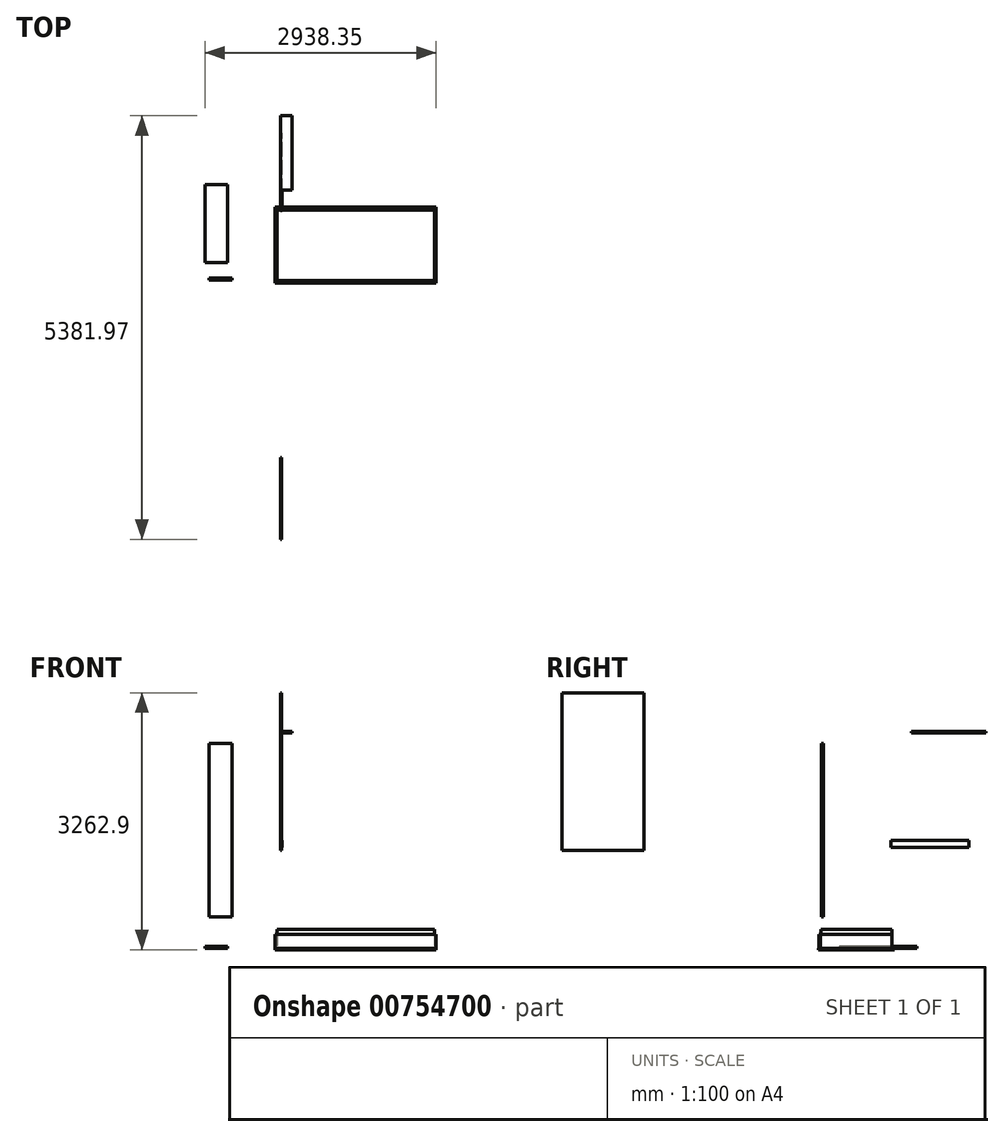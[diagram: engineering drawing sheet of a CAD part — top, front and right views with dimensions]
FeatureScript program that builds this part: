
annotation { "Feature Type Name" : "Feature", "Feature Type Description" : "" }
export const myFeature = defineFeature(function(context is Context, id is Id, definition is map)
    precondition{}
    {
        {
            assignVariable(context, id + "F0", {"name" : "MattD", "anyValue" : 240});
        }
        {
            assignVariable(context, id + "F1", {"name" : "BaseD", "anyValue" : 18});
        }
        {
            assignVariable(context, id + "F2", {"name" : "RailD", "anyValue" : 18});
        }
        {
            assignVariable(context, id + "F3", {"name" : "RailSOH", "anyValue" : 10});
        }
        {
            assignVariable(context, id + "F4", {"name" : "FrameD", "anyValue" : 24});
        }
        {
            var Q0;
            Q0=qCreatedBy(makeId("Top.planeOp"),FACE);
            var sketch = newSketch(context, id + "F5", { "sketchPlane" : qUnion([Q0])});
            skLineSegment(sketch, "E0.bottom", {"start": v(-44.22, 868.08) * mm, "end": v(1955.78, 868.08) * mm});
            skLineSegment(sketch, "E0.top", {"start": v(-44.22, -31.92) * mm, "end": v(1955.78, -31.92) * mm});
            skLineSegment(sketch, "E0.left", {"start": v(-44.22, 868.08) * mm, "end": v(-44.22, -31.92) * mm});
            skLineSegment(sketch, "E0.right", {"start": v(1955.78, 868.08) * mm, "end": v(1955.78, -31.92) * mm});
            skSolve(sketch);
        }
        {
            var Q0;
            Q0=makeQuery(id+"F5.imprint","IMPRINT",FACE,{"disambiguationData":[TD([[makeQuery(id+"F5.imprint","IMPRINT",EDGE,{"derivedFrom":sQuery(id+"F5.wireOp",EDGE,"E0.bottom")}),-1.0]])]});
            extrude(context, id + "F6", {"entities" : qUnion([Q0]), "depth" : (getVariable(context, 'MattD')) * mm, "offsetDistance" : 25 * mm});
        }
        {
            var Q0;
            Q0=qCreatedBy(makeId("Top.planeOp"),FACE);
            var sketch = newSketch(context, id + "F7", { "sketchPlane" : qUnion([Q0])});
            skLineSegment(sketch, "E1.bottom", {"start": v(-67.22, 901.08) * mm, "end": v(1978.78, 901.08) * mm});
            skLineSegment(sketch, "E1.top", {"start": v(-67.22, -64.92) * mm, "end": v(1978.78, -64.92) * mm});
            skLineSegment(sketch, "E1.left", {"start": v(-67.22, 901.08) * mm, "end": v(-67.22, -64.92) * mm});
            skLineSegment(sketch, "E1.right", {"start": v(1978.78, 901.08) * mm, "end": v(1978.78, -64.92) * mm});
            skSolve(sketch);
        }
        {
            var Q0;
            Q0=makeQuery(id+"F7.imprint","IMPRINT",FACE,{"disambiguationData":[TD([[makeQuery(id+"F7.imprint","IMPRINT",EDGE,{"derivedFrom":sQuery(id+"F7.wireOp",EDGE,"E1.bottom")}),-1.0]])]});
            extrude(context, id + "F8", {"entities" : qUnion([Q0]), "oppositeDirection" : true, "depth" : (getVariable(context, 'BaseD')) * mm, "offsetDistance" : 25 * mm});
        }
        {
            var Q0;
            Q0=makeQuery(id+"F8.opExtrude","SWEPT_FACE",FACE,{"disambiguationData":[OSD([sQuery(id+"F7.wireOp",EDGE,"E1.top")])]});
            cPlane(context, id + "F9", {"entities" : qUnion([Q0]), "cplaneType" : CPlaneType.OFFSET, "offset" : (getVariable(context, 'RailSOH')) * mm, "oppositeDirection" : true, "width" : 150 * mm, "height" : 150 * mm});
        }
        {
            var Q0;
            Q0=qCreatedBy(id+"F9.planeOp",FACE);
            var sketch = newSketch(context, id + "F10", { "sketchPlane" : qUnion([Q0])});
            skLineSegment(sketch, "E2.bottom", {"start": v(-67.22, 180) * mm, "end": v(1978.78, 180) * mm});
            skLineSegment(sketch, "E2.top", {"start": v(-67.22, 0) * mm, "end": v(1978.78, 0) * mm});
            skLineSegment(sketch, "E2.left", {"start": v(-67.22, 180) * mm, "end": v(-67.22, 0) * mm});
            skLineSegment(sketch, "E2.right", {"start": v(1978.78, 180) * mm, "end": v(1978.78, 0) * mm});
            skSolve(sketch);
        }
        {
            var Q0;
            Q0=makeQuery(id+"F10.imprint","IMPRINT",FACE,{"disambiguationData":[TD([[makeQuery(id+"F10.imprint","IMPRINT",EDGE,{"derivedFrom":sQuery(id+"F10.wireOp",EDGE,"E2.bottom")}),-1.0]])]});
            extrude(context, id + "F11", {"entities" : qUnion([Q0]), "oppositeDirection" : true, "depth" : (getVariable(context, 'RailD')) * mm, "offsetDistance" : 25 * mm});
        }
        {
            var Q0;
            Q0=makeQuery(id+"F11.opExtrude","SWEPT_FACE",FACE,{"disambiguationData":[OSD([sQuery(id+"F10.wireOp",EDGE,"E2.right")])]});
            var sketch = newSketch(context, id + "F12", { "sketchPlane" : qUnion([Q0])});
            skLineSegment(sketch, "E3.bottom", {"start": v(-36.92, 180) * mm, "end": v(873.08, 180) * mm});
            skLineSegment(sketch, "E3.top", {"start": v(-36.92, 0) * mm, "end": v(873.08, 0) * mm});
            skLineSegment(sketch, "E3.left", {"start": v(-36.92, 180) * mm, "end": v(-36.92, 0) * mm});
            skLineSegment(sketch, "E3.right", {"start": v(873.08, 180) * mm, "end": v(873.08, 0) * mm});
            skSolve(sketch);
        }
        {
            var Q0;
            Q0=makeQuery(id+"F12.imprint","IMPRINT",FACE,{"disambiguationData":[TD([[makeQuery(id+"F12.imprint","IMPRINT",EDGE,{"derivedFrom":sQuery(id+"F12.wireOp",EDGE,"E3.bottom")}),-1.0]])]});
            extrude(context, id + "F13", {"entities" : qUnion([Q0]), "oppositeDirection" : true, "depth" : (getVariable(context, 'RailD')) * mm, "offsetDistance" : 25 * mm});
        }
        {
            var Q0;
            Q0=qCreatedBy(makeId("Front.planeOp"),FACE);
            var sketch = newSketch(context, id + "F14", { "sketchPlane" : qUnion([Q0])});
            skLineSegment(sketch, "E4.bottom", {"start": v(-906.66, 2600.68) * mm, "end": v(-616.66, 2600.68) * mm});
            skLineSegment(sketch, "E4.top", {"start": v(-906.66, 400.68) * mm, "end": v(-616.66, 400.68) * mm});
            skLineSegment(sketch, "E4.left", {"start": v(-906.66, 2600.68) * mm, "end": v(-906.66, 400.68) * mm});
            skLineSegment(sketch, "E4.right", {"start": v(-616.66, 2600.68) * mm, "end": v(-616.66, 400.68) * mm});
            skSolve(sketch);
        }
        {
            var Q0;
            Q0=makeQuery(id+"F14.imprint","IMPRINT",FACE,{"disambiguationData":[TD([[makeQuery(id+"F14.imprint","IMPRINT",EDGE,{"derivedFrom":sQuery(id+"F14.wireOp",EDGE,"E4.bottom")}),-1.0]])]});
            extrude(context, id + "F15", {"entities" : qUnion([Q0]), "depth" : (getVariable(context, 'FrameD')) * mm, "offsetDistance" : 25 * mm});
        }
        {
            var Q0;
            Q0=qCreatedBy(makeId("Top.planeOp"),FACE);
            var sketch = newSketch(context, id + "F16", { "sketchPlane" : qUnion([Q0])});
            skLineSegment(sketch, "E5.bottom", {"start": v(-959.57, 1191.2) * mm, "end": v(-669.57, 1191.2) * mm});
            skLineSegment(sketch, "E5.top", {"start": v(-959.57, 201.2) * mm, "end": v(-669.57, 201.2) * mm});
            skLineSegment(sketch, "E5.left", {"start": v(-959.57, 1191.2) * mm, "end": v(-959.57, 201.2) * mm});
            skLineSegment(sketch, "E5.right", {"start": v(-669.57, 1191.2) * mm, "end": v(-669.57, 201.2) * mm});
            skSolve(sketch);
        }
        {
            var Q0;
            Q0=makeQuery(id+"F16.imprint","IMPRINT",FACE,{"disambiguationData":[TD([[makeQuery(id+"F16.imprint","IMPRINT",EDGE,{"derivedFrom":sQuery(id+"F16.wireOp",EDGE,"E5.bottom")}),-1.0]])]});
            extrude(context, id + "F17", {"entities" : qUnion([Q0]), "depth" : (getVariable(context, 'FrameD')) * mm, "offsetDistance" : 25 * mm});
        }
        {
            var Q0;
            Q0=qCreatedBy(makeId("Right.planeOp"),FACE);
            var sketch = newSketch(context, id + "F18", { "sketchPlane" : qUnion([Q0])});
            skLineSegment(sketch, "E6.bottom", {"start": v(855.86, 1371.21) * mm, "end": v(1845.86, 1371.21) * mm});
            skLineSegment(sketch, "E6.top", {"start": v(855.86, 1281.21) * mm, "end": v(1845.86, 1281.21) * mm});
            skLineSegment(sketch, "E6.left", {"start": v(855.86, 1371.21) * mm, "end": v(855.86, 1281.21) * mm});
            skLineSegment(sketch, "E6.right", {"start": v(1845.86, 1371.21) * mm, "end": v(1845.86, 1281.21) * mm});
            skSolve(sketch);
        }
        {
            var Q0;
            Q0=makeQuery(id+"F18.imprint","IMPRINT",FACE,{"disambiguationData":[TD([[makeQuery(id+"F18.imprint","IMPRINT",EDGE,{"derivedFrom":sQuery(id+"F18.wireOp",EDGE,"E6.bottom")}),-1.0]])]});
            extrude(context, id + "F19", {"entities" : qUnion([Q0]), "depth" : (getVariable(context, 'RailD')) * mm, "offsetDistance" : 25 * mm});
        }
        {
            var Q0;
            Q0=qCreatedBy(makeId("Right.planeOp"),FACE);
            var sketch = newSketch(context, id + "F20", { "sketchPlane" : qUnion([Q0])});
            skLineSegment(sketch, "E7.bottom", {"start": v(1117.42, 2758.34) * mm, "end": v(2063.42, 2758.34) * mm});
            skLineSegment(sketch, "E7.top", {"start": v(1117.42, 2734.34) * mm, "end": v(2063.42, 2734.34) * mm});
            skLineSegment(sketch, "E7.left", {"start": v(1117.42, 2758.34) * mm, "end": v(1117.42, 2734.34) * mm});
            skLineSegment(sketch, "E7.right", {"start": v(2063.42, 2758.34) * mm, "end": v(2063.42, 2734.34) * mm});
            skSolve(sketch);
        }
        {
            var Q0;
            Q0=makeQuery(id+"F20.imprint","IMPRINT",FACE,{"disambiguationData":[TD([[makeQuery(id+"F20.imprint","IMPRINT",EDGE,{"derivedFrom":sQuery(id+"F20.wireOp",EDGE,"E7.bottom")}),-1.0]])]});
            extrude(context, id + "F21", {"entities" : qUnion([Q0]), "depth" : 145 * mm, "offsetDistance" : 25 * mm});
        }
        {
            var Q0;
            Q0=qCreatedBy(makeId("Right.planeOp"),FACE);
            var sketch = newSketch(context, id + "F22", { "sketchPlane" : qUnion([Q0])});
            skLineSegment(sketch, "E8.bottom", {"start": v(-3318.55, 3244.9) * mm, "end": v(-2280.55, 3244.9) * mm});
            skLineSegment(sketch, "E8.top", {"start": v(-3318.55, 1244.9) * mm, "end": v(-2280.55, 1244.9) * mm});
            skLineSegment(sketch, "E8.left", {"start": v(-3318.55, 3244.9) * mm, "end": v(-3318.55, 1244.9) * mm});
            skLineSegment(sketch, "E8.right", {"start": v(-2280.55, 3244.9) * mm, "end": v(-2280.55, 1244.9) * mm});
            skSolve(sketch);
        }
        {
            var Q0;
            Q0=makeQuery(id+"F22.imprint","IMPRINT",FACE,{"disambiguationData":[TD([[makeQuery(id+"F22.imprint","IMPRINT",EDGE,{"derivedFrom":sQuery(id+"F22.wireOp",EDGE,"E8.bottom")}),-1.0]])]});
            extrude(context, id + "F23", {"entities" : qUnion([Q0]), "depth" : 15 * mm, "offsetDistance" : 25 * mm});
        }
    });
